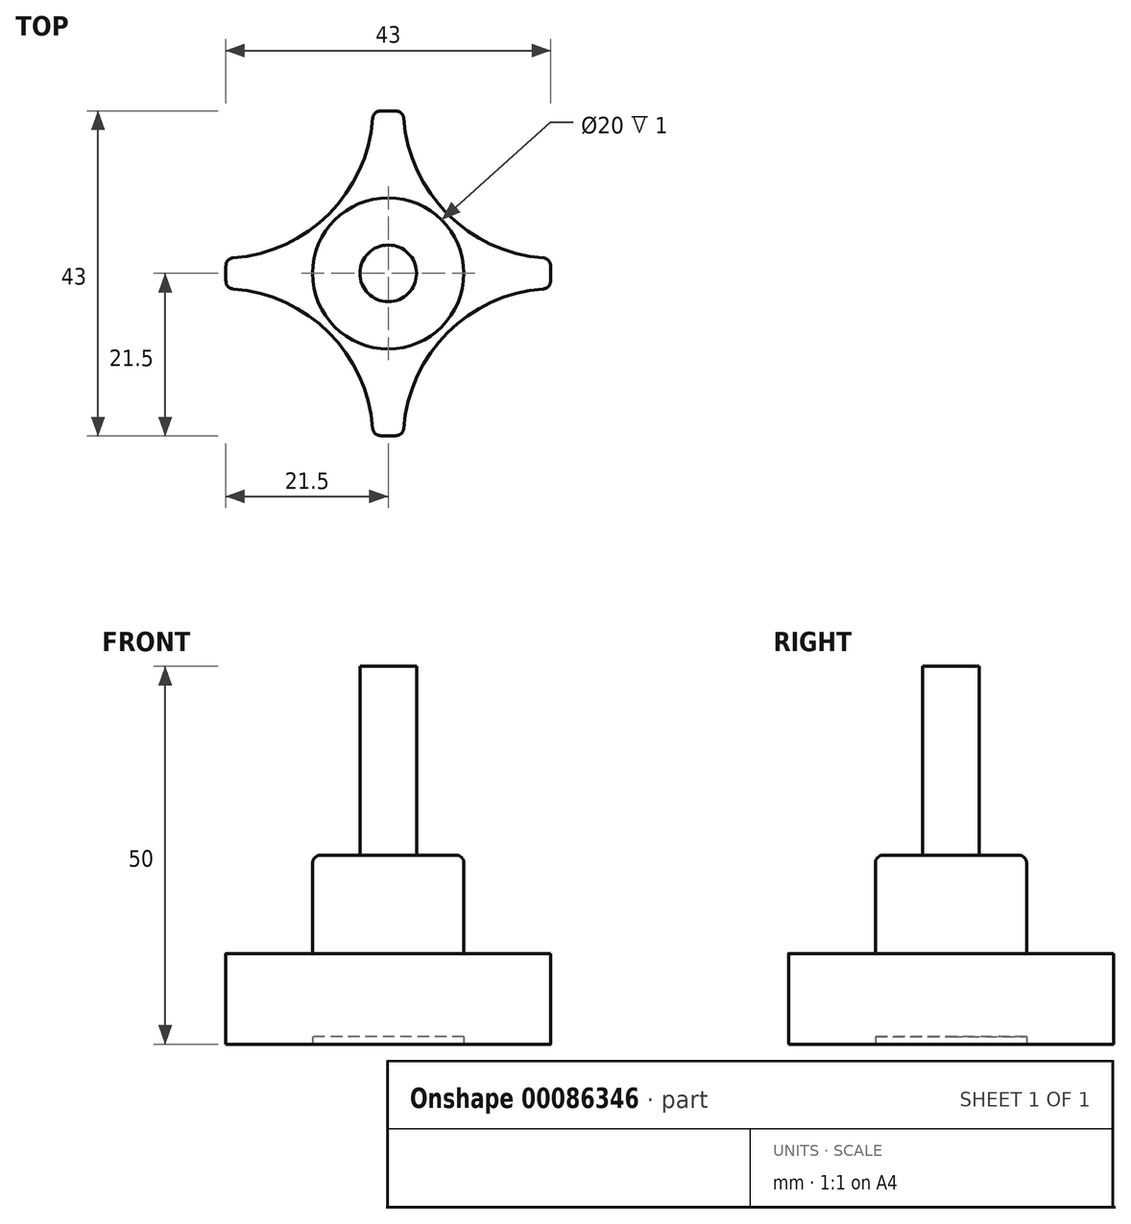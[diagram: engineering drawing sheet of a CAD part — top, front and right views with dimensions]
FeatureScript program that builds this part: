
annotation { "Feature Type Name" : "Feature", "Feature Type Description" : "" }
export const myFeature = defineFeature(function(context is Context, id is Id, definition is map)
    precondition{}
    {
        {
            var Q0;
            Q0=qCreatedBy(makeId("Top.planeOp"),FACE);
            var sketch = newSketch(context, id + "F0", { "sketchPlane" : qUnion([Q0])});
            skArc(sketch, "E0", {"start": v(-21.4, 2) * mm, "mid": v(-21.5, 0) * mm, "end": v(-21.4, -2) * mm});
            skArc(sketch, "E1", {"start": v(-21.4, 2) * mm, "mid": v(-7.85, 7.85) * mm, "end": v(-2, 21.4) * mm});
            skArc(sketch, "E2.MirrorCS", {"start": v(21.4, 2) * mm, "mid": v(7.85, 7.85) * mm, "end": v(2, 21.4) * mm});
            skArc(sketch, "E3.MirrorCS", {"start": v(21.4, -2) * mm, "mid": v(7.85, -7.85) * mm, "end": v(2, -21.4) * mm});
            skArc(sketch, "E4.MirrorCS", {"start": v(-21.4, -2) * mm, "mid": v(-7.85, -7.85) * mm, "end": v(-2, -21.4) * mm});
            skCircle(sketch, "E5", {"center": v(0, 0) * mm, "radius": 10 * mm});
            skPoint(sketch, "E6.end.orphan", {"position": v(-2, 21.4) * mm});
            skPoint(sketch, "E7.MirrorCS.end.orphan", {"position": v(-2, -21.4) * mm});
            skPoint(sketch, "E7.MirrorCS.start.orphan", {"position": v(-21.4, -2) * mm});
            skPoint(sketch, "E8.MirrorCS.end.orphan", {"position": v(2, -21.4) * mm});
            skPoint(sketch, "E8.MirrorCS.start.orphan", {"position": v(21.4, -2) * mm});
            skPoint(sketch, "E9.MirrorCS.end.orphan", {"position": v(2, 21.4) * mm});
            skPoint(sketch, "E9.MirrorCS.start.orphan", {"position": v(21.4, 2) * mm});
            skArc(sketch, "E10.trimOffspring", {"start": v(-2, -21.4) * mm, "mid": v(0, -21.5) * mm, "end": v(2, -21.4) * mm});
            skArc(sketch, "E11.trimOffspring", {"start": v(21.4, -2) * mm, "mid": v(21.5, 0) * mm, "end": v(21.4, 2) * mm});
            skArc(sketch, "E12.trimOffspring", {"start": v(2, 21.4) * mm, "mid": v(0, 21.5) * mm, "end": v(-2, 21.4) * mm});
            skSolve(sketch);
        }
        {
            var Q0;
            {var subQ0=sQuery(id+"F0.wireOp",EDGE,"E2.MirrorCS");Q0=makeQuery(id+"F0.imprint","IMPRINT",FACE,{"disambiguationData":[TD([[makeQuery(id+"F0.imprint","IMPRINT",EDGE,{"derivedFrom":subQ0}),-1.0]])]});}
            var Q1;
            {var subQ0=sQuery(id+"F0.wireOp",EDGE,"E4.MirrorCS");Q1=makeQuery(id+"F0.imprint","IMPRINT",FACE,{"disambiguationData":[TD([[makeQuery(id+"F0.imprint","IMPRINT",EDGE,{"derivedFrom":subQ0}),-1.0]])]});}
            var Q2;
            {var subQ0=sQuery(id+"F0.wireOp",EDGE,"E3.MirrorCS");Q2=makeQuery(id+"F0.imprint","IMPRINT",FACE,{"disambiguationData":[TD([[makeQuery(id+"F0.imprint","IMPRINT",EDGE,{"derivedFrom":subQ0}),1.0]])]});}
            var Q3;
            {var subQ4=sQuery(id+"F0.wireOp",EDGE,"E1");Q3=makeQuery(id+"F0.imprint","IMPRINT",FACE,{"disambiguationData":[TD([[makeQuery(id+"F0.imprint","IMPRINT",EDGE,{"derivedFrom":subQ4}),-1.0]])]});}
            var Q4;
            Q4=makeQuery(id+"F0.imprint","IMPRINT",FACE,{"disambiguationData":[TD([[makeQuery(id+"F0.imprint","IMPRINT",EDGE,{"derivedFrom":sQuery(id+"F0.wireOp",EDGE,"E5")}),1.0]])]});
            var Q5;
            {var subQ0=sQuery(id+"F0.wireOp",EDGE,"E1");Q5=makeQuery(id+"F0.imprint","IMPRINT",FACE,{"disambiguationData":[TD([[makeQuery(id+"F0.imprint","IMPRINT",EDGE,{"derivedFrom":subQ0}),1.0]])]});}
            extrude(context, id + "F1", {"entities" : qUnion([Q0, Q1, Q2, Q3, Q4, Q5]), "depth" : 12 * mm});
        }
        {
            var Q0;
            Q0=makeQuery(id+"F1.opExtrude","CAP_FACE",FACE,{"disambiguationData":[OSD([sQuery(id+"F0.wireOp",EDGE,"E0")])],"isStart":false});
            var sketch = newSketch(context, id + "F2", { "sketchPlane" : qUnion([Q0])});
            skCircle(sketch, "E13", {"center": v(0, 0) * mm, "radius": 10 * mm});
            skSolve(sketch);
        }
        {
            var Q0;
            Q0 = qSketchRegion(id + "F2", true);
            extrude(context, id + "F3", {"entities" : qUnion([Q0]), "operationType" : NewBodyOperationType.ADD, "depth" : 13 * mm});
        }
        {
            var Q0;
            Q0=makeQuery(id+"F3.opExtrude","CAP_FACE",FACE,{"disambiguationData":[OSD([sQuery(id+"F2.wireOp",EDGE,"E13")])],"isStart":false});
            var sketch = newSketch(context, id + "F4", { "sketchPlane" : qUnion([Q0])});
            skCircle(sketch, "E14", {"center": v(0, 0) * mm, "radius": 3.75 * mm});
            skSolve(sketch);
        }
        {
            var Q0;
            Q0 = qSketchRegion(id + "F4", true);
            extrude(context, id + "F5", {"entities" : qUnion([Q0]), "operationType" : NewBodyOperationType.ADD, "depth" : 25 * mm});
        }
        {
            var Q0;
            Q0=makeQuery(id+"F3.opExtrude","CAP_EDGE",EDGE,{"disambiguationData":[OSD([sQuery(id+"F2.wireOp",EDGE,"E13")])],"isStart":false});
            fillet(context, id + "F6", {"entities" : qUnion([Q0]), "radius" : 1 * mm, "tangentPropagation" : true, "allowEdgeOverflow" : false});
        }
        {
            var Q0;
            {var subQ0=sQuery(id+"F0.wireOp",EDGE,"E2.MirrorCS");var subQ1=sQuery(id+"F0.wireOp",EDGE,"E0");Q0=makeQuery(id+"F2CR9NZCdlHnQEh_0.boolean.opBoolean","COPY",EDGE,{"derivedFrom":makeQuery(id+"F2CR9NZCdlHnQEh_0.opExtrude","SWEPT_EDGE",EDGE,{"disambiguationData":[OSD([subQ1,subQ0]),TDD([makeQuery(id+"F0.imprint","INTERSECT",VERTEX,{"disambiguationData":[OD(0.0)],"derivedFrom":[subQ1,subQ0]})])]})});}
            var Q1;
            {var subQ0=sQuery(id+"F0.wireOp",EDGE,"E3.MirrorCS");var subQ1=sQuery(id+"F0.wireOp",EDGE,"E0");Q1=makeQuery(id+"F2CR9NZCdlHnQEh_0.boolean.opBoolean","COPY",EDGE,{"derivedFrom":makeQuery(id+"F2CR9NZCdlHnQEh_0.opExtrude","SWEPT_EDGE",EDGE,{"disambiguationData":[OSD([subQ1,subQ0]),TDD([makeQuery(id+"F0.imprint","INTERSECT",VERTEX,{"disambiguationData":[OD(0.0)],"derivedFrom":[subQ1,subQ0]})])]})});}
            var Q2;
            {var subQ0=sQuery(id+"F0.wireOp",EDGE,"E2.MirrorCS");var subQ1=sQuery(id+"F0.wireOp",EDGE,"E0");Q2=makeQuery(id+"F2CR9NZCdlHnQEh_0.boolean.opBoolean","COPY",EDGE,{"derivedFrom":makeQuery(id+"F2CR9NZCdlHnQEh_0.opExtrude","SWEPT_EDGE",EDGE,{"disambiguationData":[OSD([subQ1,subQ0]),TDD([makeQuery(id+"F0.imprint","INTERSECT",VERTEX,{"disambiguationData":[OD(1.0)],"derivedFrom":[subQ1,subQ0]})])]})});}
            var Q3;
            {var subQ0=sQuery(id+"F0.wireOp",EDGE,"E1");var subQ1=sQuery(id+"F0.wireOp",EDGE,"E0");Q3=makeQuery(id+"F2CR9NZCdlHnQEh_0.boolean.opBoolean","COPY",EDGE,{"derivedFrom":makeQuery(id+"F2CR9NZCdlHnQEh_0.opExtrude","SWEPT_EDGE",EDGE,{"disambiguationData":[OSD([subQ1,subQ0]),TDD([makeQuery(id+"F0.imprint","INTERSECT",VERTEX,{"disambiguationData":[OD(1.0)],"derivedFrom":[subQ1,subQ0]})])]})});}
            var Q4;
            {var subQ0=sQuery(id+"F0.wireOp",EDGE,"E4.MirrorCS");var subQ1=sQuery(id+"F0.wireOp",EDGE,"E0");Q4=makeQuery(id+"F2CR9NZCdlHnQEh_0.boolean.opBoolean","COPY",EDGE,{"derivedFrom":makeQuery(id+"F2CR9NZCdlHnQEh_0.opExtrude","SWEPT_EDGE",EDGE,{"disambiguationData":[OSD([subQ1,subQ0]),TDD([makeQuery(id+"F0.imprint","INTERSECT",VERTEX,{"disambiguationData":[OD(0.0)],"derivedFrom":[subQ1,subQ0]})])]})});}
            var Q5;
            {var subQ0=sQuery(id+"F0.wireOp",EDGE,"E4.MirrorCS");var subQ1=sQuery(id+"F0.wireOp",EDGE,"E0");Q5=makeQuery(id+"F2CR9NZCdlHnQEh_0.boolean.opBoolean","COPY",EDGE,{"derivedFrom":makeQuery(id+"F2CR9NZCdlHnQEh_0.opExtrude","SWEPT_EDGE",EDGE,{"disambiguationData":[OSD([subQ1,subQ0]),TDD([makeQuery(id+"F0.imprint","INTERSECT",VERTEX,{"disambiguationData":[OD(1.0)],"derivedFrom":[subQ1,subQ0]})])]})});}
            var Q6;
            {var subQ0=sQuery(id+"F0.wireOp",EDGE,"E3.MirrorCS");var subQ1=sQuery(id+"F0.wireOp",EDGE,"E0");Q6=makeQuery(id+"F2CR9NZCdlHnQEh_0.boolean.opBoolean","COPY",EDGE,{"derivedFrom":makeQuery(id+"F2CR9NZCdlHnQEh_0.opExtrude","SWEPT_EDGE",EDGE,{"disambiguationData":[OSD([subQ1,subQ0]),TDD([makeQuery(id+"F0.imprint","INTERSECT",VERTEX,{"disambiguationData":[OD(1.0)],"derivedFrom":[subQ1,subQ0]})])]})});}
            var Q7;
            {var subQ0=sQuery(id+"F0.wireOp",EDGE,"E1");var subQ1=sQuery(id+"F0.wireOp",EDGE,"E0");Q7=makeQuery(id+"F2CR9NZCdlHnQEh_0.boolean.opBoolean","COPY",EDGE,{"derivedFrom":makeQuery(id+"F2CR9NZCdlHnQEh_0.opExtrude","SWEPT_EDGE",EDGE,{"disambiguationData":[OSD([subQ1,subQ0]),TDD([makeQuery(id+"F0.imprint","INTERSECT",VERTEX,{"disambiguationData":[OD(0.0)],"derivedFrom":[subQ1,subQ0]})])]})});}
            var Q8;
            Q8=makeQuery(id+"F1.opExtrude","SWEPT_EDGE",EDGE,{"disambiguationData":[OSD([sQuery(id+"F0.wireOp",EDGE,"E4.MirrorCS"),sQuery(id+"F0.wireOp",EDGE,"E10.trimOffspring")])]});
            var Q9;
            Q9=makeQuery(id+"F1.opExtrude","SWEPT_EDGE",EDGE,{"disambiguationData":[OSD([sQuery(id+"F0.wireOp",EDGE,"E3.MirrorCS"),sQuery(id+"F0.wireOp",EDGE,"E10.trimOffspring")])]});
            var Q10;
            Q10=makeQuery(id+"F1.opExtrude","SWEPT_EDGE",EDGE,{"disambiguationData":[OSD([sQuery(id+"F0.wireOp",EDGE,"E0"),sQuery(id+"F0.wireOp",EDGE,"E4.MirrorCS")])]});
            var Q11;
            Q11=makeQuery(id+"F1.opExtrude","SWEPT_EDGE",EDGE,{"disambiguationData":[OSD([sQuery(id+"F0.wireOp",EDGE,"E0"),sQuery(id+"F0.wireOp",EDGE,"E1")])]});
            var Q12;
            Q12=makeQuery(id+"F1.opExtrude","SWEPT_EDGE",EDGE,{"disambiguationData":[OSD([sQuery(id+"F0.wireOp",EDGE,"E1"),sQuery(id+"F0.wireOp",EDGE,"E12.trimOffspring")])]});
            var Q13;
            Q13=makeQuery(id+"F1.opExtrude","SWEPT_EDGE",EDGE,{"disambiguationData":[OSD([sQuery(id+"F0.wireOp",EDGE,"E2.MirrorCS"),sQuery(id+"F0.wireOp",EDGE,"E12.trimOffspring")])]});
            var Q14;
            Q14=makeQuery(id+"F1.opExtrude","SWEPT_EDGE",EDGE,{"disambiguationData":[OSD([sQuery(id+"F0.wireOp",EDGE,"E2.MirrorCS"),sQuery(id+"F0.wireOp",EDGE,"E11.trimOffspring")])]});
            var Q15;
            Q15=makeQuery(id+"F1.opExtrude","SWEPT_EDGE",EDGE,{"disambiguationData":[OSD([sQuery(id+"F0.wireOp",EDGE,"E3.MirrorCS"),sQuery(id+"F0.wireOp",EDGE,"E11.trimOffspring")])]});
            fillet(context, id + "F7", {"entities" : qUnion([Q0, Q1, Q2, Q3, Q4, Q5, Q6, Q7, Q8, Q9, Q10, Q11, Q12, Q13, Q14, Q15]), "radius" : 1 * mm, "tangentPropagation" : true, "allowEdgeOverflow" : false});
        }
        {
            var Q0;
            Q0=makeQuery(id+"F0.imprint","IMPRINT",FACE,{"disambiguationData":[TD([[makeQuery(id+"F0.imprint","IMPRINT",EDGE,{"derivedFrom":sQuery(id+"F0.wireOp",EDGE,"E5")}),1.0]])]});
            extrude(context, id + "F8", {"entities" : qUnion([Q0]), "operationType" : NewBodyOperationType.REMOVE, "depth" : 1 * mm});
        }
    });
